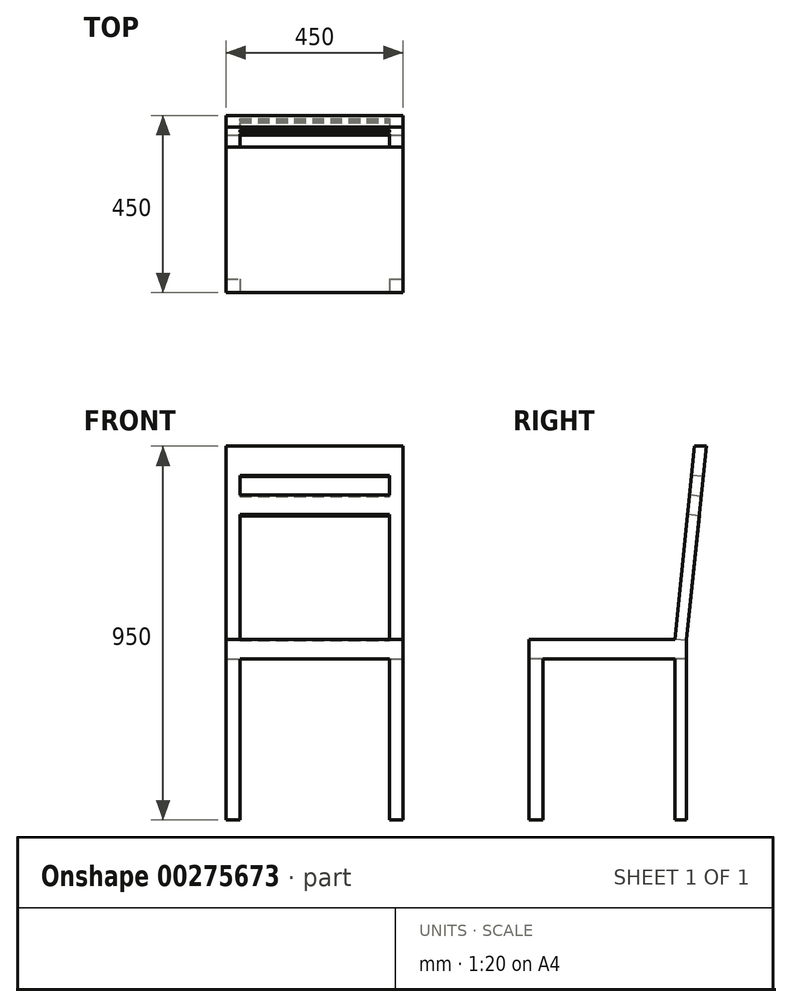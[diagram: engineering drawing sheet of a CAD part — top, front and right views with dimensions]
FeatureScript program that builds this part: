
annotation { "Feature Type Name" : "Feature", "Feature Type Description" : "" }
export const myFeature = defineFeature(function(context is Context, id is Id, definition is map)
    precondition{}
    {
        {
            var Q0;
            Q0=qCreatedBy(makeId("Top.planeOp"),FACE);
            var sketch = newSketch(context, id + "F0", { "sketchPlane" : qUnion([Q0])});
            skLineSegment(sketch, "E0.bottom", {"start": v(225, 225) * mm, "end": v(-225, 225) * mm});
            skLineSegment(sketch, "E0.top", {"start": v(225, -225) * mm, "end": v(-225, -225) * mm});
            skLineSegment(sketch, "E0.left", {"start": v(225, 225) * mm, "end": v(225, -225) * mm});
            skLineSegment(sketch, "E0.right", {"start": v(-225, 225) * mm, "end": v(-225, -225) * mm});
            skPoint(sketch, "E0.middle", {"position": v(0, 0) * mm});
            skSolve(sketch);
        }
        {
            var Q0;
            Q0=qSketchRegion(id+"F0",true);
            extrude(context, id + "F1", {"entities" : qUnion([Q0]), "depth" : 950 * mm});
        }
        {
            var Q0;
            Q0=makeQuery(id+"F1.opExtrude","SWEPT_FACE",FACE,{"disambiguationData":[OSD([sQuery(id+"F0.wireOp",EDGE,"E0.left")])]});
            var sketch = newSketch(context, id + "F2", { "sketchPlane" : qUnion([Q0])});
            skLineSegment(sketch, "E1.bottom", {"start": v(-225, 459.07) * mm, "end": v(225, 459.07) * mm});
            skLineSegment(sketch, "E1.top", {"start": v(-225, 409.07) * mm, "end": v(225, 409.07) * mm});
            skLineSegment(sketch, "E1.left", {"start": v(-225, 459.07) * mm, "end": v(-225, 409.07) * mm});
            skLineSegment(sketch, "E1.right", {"start": v(225, 459.07) * mm, "end": v(225, 409.07) * mm});
            skLineSegment(sketch, "E2", {"start": v(225, 950) * mm, "end": v(175, 459.07) * mm});
            skLineSegment(sketch, "E3", {"start": v(195, 950) * mm, "end": v(145, 459.07) * mm});
            skLineSegment(sketch, "E4", {"start": v(175, 459.07) * mm, "end": v(175, 0) * mm});
            skLineSegment(sketch, "E5", {"start": v(145, 459.07) * mm, "end": v(145, 0) * mm});
            skLineSegment(sketch, "E6.bottom", {"start": v(-225, 409.07) * mm, "end": v(-190, 409.07) * mm});
            skLineSegment(sketch, "E6.top", {"start": v(-225, 0) * mm, "end": v(-190, 0) * mm});
            skLineSegment(sketch, "E6.left", {"start": v(-225, 409.07) * mm, "end": v(-225, 0) * mm});
            skLineSegment(sketch, "E6.right", {"start": v(-190, 409.07) * mm, "end": v(-190, 0) * mm});
            skSolve(sketch);
        }
        {
            var Q0;
            {var subQ4=sQuery(id+"F2.wireOp",EDGE,"E2");Q0=makeQuery(id+"F2.imprint","IMPRINT",FACE,{"disambiguationData":[TD([[makeQuery(id+"F2.imprint","IMPRINT",EDGE,{"derivedFrom":subQ4}),1.0]])]});}
            var Q1;
            {var subQ4=sQuery(id+"F2.wireOp",EDGE,"E3");Q1=makeQuery(id+"F2.imprint","IMPRINT",FACE,{"disambiguationData":[TD([[makeQuery(id+"F2.imprint","IMPRINT",EDGE,{"derivedFrom":subQ4}),-1.0]])]});}
            var Q2;
            {var subQ1=sQuery(id+"F0.wireOp",EDGE,"E0.left");var subQ4=sQuery(id+"F2.wireOp",EDGE,"E4");var subQ6=makeQuery(id+"F1.opExtrude","CAP_EDGE",EDGE,{"disambiguationData":[OSD([subQ1])],"isStart":true});var subQ7=makeQuery(id+"F2.imprint","INTERSECT",VERTEX,{"derivedFrom":[subQ6,subQ4]});Q2=makeQuery(id+"F2.imprint","IMPRINT",FACE,{"disambiguationData":[TD([[makeQuery(id+"F2.imprint","IMPRINT",EDGE,{"disambiguationData":[TD([[subQ7,1.0]])],"derivedFrom":subQ4}),1.0]])]});}
            var Q3;
            {var subQ0=sQuery(id+"F2.wireOp",EDGE,"E6.right");Q3=makeQuery(id+"F2.imprint","IMPRINT",FACE,{"disambiguationData":[TD([[makeQuery(id+"F2.imprint","IMPRINT",EDGE,{"derivedFrom":subQ0}),1.0]])]});}
            var Q4;
            {var subQ0=sQuery(id+"F2.wireOp",EDGE,"E1.right");Q4=makeQuery(id+"F2.imprint","IMPRINT",FACE,{"disambiguationData":[TD([[makeQuery(id+"F2.imprint","IMPRINT",EDGE,{"derivedFrom":subQ0}),-1.0]])]});}
            extrude(context, id + "F3", {"entities" : qUnion([Q0, Q1, Q2, Q3, Q4]), "operationType" : NewBodyOperationType.REMOVE, "endBound" : BoundingType.THROUGH_ALL, "oppositeDirection" : true, "depth" : 25 * mm});
        }
        {
            var Q0;
            Q0=makeQuery(id+"F1.opExtrude","SWEPT_FACE",FACE,{"disambiguationData":[OSD([sQuery(id+"F0.wireOp",EDGE,"E0.top")])]});
            var sketch = newSketch(context, id + "F4", { "sketchPlane" : qUnion([Q0])});
            skLineSegment(sketch, "E7", {"start": v(-190, 0) * mm, "end": v(-190, 409.07) * mm});
            skLineSegment(sketch, "E8", {"start": v(-190, 409.07) * mm, "end": v(190, 409.07) * mm});
            skLineSegment(sketch, "E9", {"start": v(190, 409.07) * mm, "end": v(190, 0) * mm});
            skSolve(sketch);
        }
        {
            var Q0;
            Q0 = qSketchRegion(id + "F4", true);
            var Q1;
            {var subQ0=sQuery(id+"F4.wireOp",EDGE,"E7");Q1=makeQuery(id+"F4.imprint","IMPRINT",FACE,{"disambiguationData":[TD([[makeQuery(id+"F4.imprint","IMPRINT",EDGE,{"derivedFrom":subQ0}),-1.0]])]});}
            extrude(context, id + "F5", {"entities" : qUnion([Q0, Q1]), "operationType" : NewBodyOperationType.REMOVE, "endBound" : BoundingType.THROUGH_ALL, "oppositeDirection" : true, "depth" : 25 * mm});
        }
        {
            var Q0;
            Q0=makeQuery(id+"F3.boolean.opBoolean","COPY",FACE,{"derivedFrom":makeQuery(id+"F3.opExtrude","SWEPT_FACE",FACE,{"disambiguationData":[OSD([sQuery(id+"F2.wireOp",EDGE,"E3")])]})});
            var sketch = newSketch(context, id + "F6", { "sketchPlane" : qUnion([Q0])});
            skLineSegment(sketch, "E10", {"start": v(-190, 471.4) * mm, "end": v(-190, 889.87) * mm});
            skLineSegment(sketch, "E11", {"start": v(-190, 889.87) * mm, "end": v(190, 889.87) * mm});
            skLineSegment(sketch, "E12", {"start": v(190, 889.87) * mm, "end": v(190, 471.4) * mm});
            skLineSegment(sketch, "E13", {"start": v(-190, 839.87) * mm, "end": v(190, 839.87) * mm});
            skLineSegment(sketch, "E14", {"start": v(-190, 789.87) * mm, "end": v(190, 789.87) * mm});
            skSolve(sketch);
        }
        {
            var Q0;
            {var subQ0=sQuery(id+"F6.wireOp",EDGE,"E11");Q0=makeQuery(id+"F6.imprint","IMPRINT",FACE,{"disambiguationData":[TD([[makeQuery(id+"F6.imprint","IMPRINT",EDGE,{"derivedFrom":subQ0}),-1.0]])]});}
            var Q1;
            {var subQ3=sQuery(id+"F6.wireOp",EDGE,"E14");Q1=makeQuery(id+"F6.imprint","IMPRINT",FACE,{"disambiguationData":[TD([[makeQuery(id+"F6.imprint","IMPRINT",EDGE,{"derivedFrom":subQ3}),-1.0]])]});}
            extrude(context, id + "F7", {"entities" : qUnion([Q0, Q1]), "operationType" : NewBodyOperationType.REMOVE, "endBound" : BoundingType.THROUGH_ALL, "oppositeDirection" : true, "depth" : 25 * mm});
        }
    });
